# Revit family: Trim-Modern_Dots-Waterworks-Universal-Thermostatic_Valve
name_source: partatom
category: Plumbing Fixtures
revit_build: Autodesk Revit MEP 2014 (Build: 20140709_2115(x64)
units: mm (PartAtom-declared; Revit-internal decimal feet)

## types (32) — shared parameters
ADA Compliant = Yes
Assembly Code = C1030200
CW Connection = No
Default Elevation = 3' - 0"
Depth = 0' - 0 3/16"
HW Connection = No
Height = 0' - 3 3/4"
Keynote = 22 40 00
Length = 0' - 3 3/4"
Manufacturer = Waterworks
Product Documentation Link = http://assets.waterworks.com
Product Page URL = http://www.waterworks.com
URL = http://www.waterworks.com
Vent Connection = No
Version = 2014 - v1.0a
Warranty = http://www.waterworks.com
Waste Connection = No
‌Installation Requirements or Notes = Valve rough-in and finished wall must be completed prior to diverter valve trim installation.

## per-type parameters (varying)
| type | Constraint | ControlM | Description | Finish | Model | Model SKU | Product Name | Three Way Diverter | Two Way Diverter |
| Two Way Diverter Antique Brass | 1 | 1 | Universal Two Way Diverter Valve Trim for Thermostatic in Antique Brass | Metal - Waterworks - Antique Brass | UN2TM1 | 05-22928-42878 | Universal Two Way Diverter Valve Trim for Thermostatic in Antique Brass | No | Yes |
| Two Way Diverter Antique Copper | 1 | 2 | Universal Two Way Diverter Valve Trim for Thermostatic in Antique Copper | Metal - Waterworks - Antique Copper | UN2TM1 | 05-36529-58078 | Universal Two Way Diverter Valve Trim for Thermostatic in Antique Copper | No | Yes |
| Two Way Diverter Architectural Bronze | 1 | 3 | Universal Two Way Diverter Valve Trim for Thermostatic in Architectural Bronze | Metal - Waterworks - Architectural Bronze | UN2TM1 | 05-01338-41785 | Universal Two Way Diverter Valve Trim for Thermostatic in Architectural Bronze | No | Yes |
| Two Way Diverter Burnished Brass | 1 | 4 | Universal Two Way Diverter Valve Trim for Thermostatic in Burnished Brass | Metal - Waterworks - Burnished Brass | UN2TM1 | 05-19937-36672 | Universal Two Way Diverter Valve Trim for Thermostatic in Burnished Brass | No | Yes |
| Two Way Diverter Burnished Nickel | 1 | 5 | Universal Two Way Diverter Valve Trim for Thermostatic in Burnished Nickel | Metal - Waterworks - Burnished Nickel | UN2TM1 | 05-37655-42558 | Universal Two Way Diverter Valve Trim for Thermostatic in Burnished Nickel | No | Yes |
| Two Way Diverter Carbon | 1 | 6 | Universal Two Way Diverter Valve Trim for Thermostatic in Carbon | Metal - Waterworks - Carbon | UN2TM1 | 05-09789-66498 | Universal Two Way Diverter Valve Trim for Thermostatic in Carbon | No | Yes |
| Two Way Diverter Chrome | 1 | 7 | Universal Two Way Diverter Valve Trim for Thermostatic in Chrome | Metal - Waterworks - Chrome | UN2TM1 | 05-77762-57694 | Universal Two Way Diverter Valve Trim for Thermostatic in Chrome | No | Yes |
| Two Way Diverter Gold | 1 | 8 | Universal Two Way Diverter Valve Trim for Thermostatic in Gold | Metal - Waterworks - Gold | UN2TM1 | 05-06073-46610 | Universal Two Way Diverter Valve Trim for Thermostatic in Gold | No | Yes |
| Two Way Diverter Matte Gold | 1 | 9 | Universal Two Way Diverter Valve Trim for Thermostatic in Matte Gold | Metal - Waterworks - Matte Gold | UN2TM1 | 05-86456-21182 | Universal Two Way Diverter Valve Trim for Thermostatic in Matte Gold | No | Yes |
| Two Way Diverter Matte Nickel | 1 | 10 | Universal Two Way Diverter Valve Trim for Thermostatic in Matte Nickel | Metal - Waterworks - Matte Nickel | UN2TM1 | 05-69705-07265 | Universal Two Way Diverter Valve Trim for Thermostatic in Matte Nickel | No | Yes |
| Two Way Diverter Nickel | 1 | 11 | Universal Two Way Diverter Valve Trim for Thermostatic in Nickel | Metal - Waterworks - Nickel | UN2TM1 | 05-23391-97102 | Universal Two Way Diverter Valve Trim for Thermostatic in Nickel | No | Yes |
| Two Way Diverter Pewter | 1 | 12 | Universal Two Way Diverter Valve Trim for Thermostatic in Pewter | Metal - Waterworks - Pewter | UN2TM1 | 05-39654-76002 | Universal Two Way Diverter Valve Trim for Thermostatic in Pewter | No | Yes |
| Two Way Diverter Shiny Copper | 1 | 13 | Universal Two Way Diverter Valve Trim for Thermostatic in Shiny Copper | Metal - Waterworks - Shiny Copper | UN2TM1 | 05-16015-99898 | Universal Two Way Diverter Valve Trim for Thermostatic in Shiny Copper | No | Yes |
| Two Way Diverter Sovereign | 1 | 14 | Universal Two Way Diverter Valve Trim for Thermostatic in Sovereign | Metal - Waterworks - Sovereign | UN2TM1 | 05-23788-55453 | Universal Two Way Diverter Valve Trim for Thermostatic in Sovereign | No | Yes |
| Two Way Diverter Unlacquered Brass | 1 | 15 | Universal Two Way Diverter Valve Trim for Thermostatic in Unlacquered Brass | Metal - Waterworks - Unlacquered Brass | UN2TM1 | 05-95064-94585 | Universal Two Way Diverter Valve Trim for Thermostatic in Unlacquered Brass | No | Yes |
| Two Way Diverter Vintage Brass | 1 | 16 | Universal Two Way Diverter Valve Trim for Thermostatic in Vintage Brass | Metal - Waterworks - Vintage Brass | UN2TM1 | 05-02148-62719 | Universal Two Way Diverter Valve Trim for Thermostatic in Vintage Brass | No | Yes |
| Three Way Diverter Antique Brass | 2 | 1 | Universal Three Way Diverter Valve Trim for Thermostatic in Antique Brass | Metal - Waterworks - Antique Brass | UN3TM1 | 05-97624-32459 | Universal Three Way Diverter Valve Trim for Thermostatic in Antique Brass | Yes | No |
| Three Way Diverter Antique Copper | 2 | 2 | Universal Three Way Diverter Valve Trim for Thermostatic in Antique Copper | Metal - Waterworks - Antique Copper | UN3TM1 | 05-24403-44214 | Universal Three Way Diverter Valve Trim for Thermostatic in Antique Copper | Yes | No |
| Three Way Diverter Architectural Bronze | 2 | 3 | Universal Three Way Diverter Valve Trim for Thermostatic in Architectural Bronze | Metal - Waterworks - Architectural Bronze | UN3TM1 | 05-26782-24273 | Universal Three Way Diverter Valve Trim for Thermostatic in Architectural Bronze | Yes | No |
| Three Way Diverter Burnished Brass | 2 | 4 | Universal Three Way Diverter Valve Trim for Thermostatic in Burnished Brass | Metal - Waterworks - Burnished Brass | UN3TM1 | 05-42249-10130 | Universal Three Way Diverter Valve Trim for Thermostatic in Burnished Brass | Yes | No |
| Three Way Diverter Burnished Nickel | 2 | 5 | Universal Three Way Diverter Valve Trim for Thermostatic in Burnished Nickel | Metal - Waterworks - Burnished Nickel | UN3TM1 | 05-16267-54630 | Universal Three Way Diverter Valve Trim for Thermostatic in Burnished Nickel | Yes | No |
| Three Way Diverter Carbon | 2 | 6 | Universal Three Way Diverter Valve Trim for Thermostatic in Carbon | Metal - Waterworks - Carbon | UN3TM1 | 05-61901-60749 | Universal Three Way Diverter Valve Trim for Thermostatic in Carbon | Yes | No |
| Three Way Diverter Chrome | 2 | 7 | Universal Three Way Diverter Valve Trim for Thermostatic in Chrome | Metal - Waterworks - Chrome | UN3TM1 | 05-28288-44779 | Universal Three Way Diverter Valve Trim for Thermostatic in Chrome | Yes | No |
| Three Way Diverter Gold | 2 | 8 | Universal Three Way Diverter Valve Trim for Thermostatic in Gold | Metal - Waterworks - Gold | UN3TM1 | 05-28626-16723 | Universal Three Way Diverter Valve Trim for Thermostatic in Gold | Yes | No |
| Three Way Diverter Matte Gold | 2 | 9 | Universal Three Way Diverter Valve Trim for Thermostatic in Matte Gold | Metal - Waterworks - Matte Gold | UN3TM1 | 05-66451-82811 | Universal Three Way Diverter Valve Trim for Thermostatic in Matte Gold | Yes | No |
| Three Way Diverter Matte Nickel | 2 | 10 | Universal Three Way Diverter Valve Trim for Thermostatic in Matte Nickel | Metal - Waterworks - Matte Nickel | UN3TM1 | 05-37432-92778 | Universal Three Way Diverter Valve Trim for Thermostatic in Matte Nickel | Yes | No |
| Three Way Diverter Nickel | 2 | 11 | Universal Three Way Diverter Valve Trim for Thermostatic in Nickel | Metal - Waterworks - Nickel | UN3TM1 | 05-60743-83830 | Universal Three Way Diverter Valve Trim for Thermostatic in Nickel | Yes | No |
| Three Way Diverter Pewter | 2 | 12 | Universal Three Way Diverter Valve Trim for Thermostatic in Pewter | Metal - Waterworks - Pewter | UN3TM1 | 05-32332-66926 | Universal Three Way Diverter Valve Trim for Thermostatic in Pewter | Yes | No |
| Three Way Diverter Shiny Copper | 2 | 13 | Universal Three Way Diverter Valve Trim for Thermostatic in Shiny Copper | Metal - Waterworks - Shiny Copper | UN3TM1 | 05-24296-38095 | Universal Three Way Diverter Valve Trim for Thermostatic in Shiny Copper | Yes | No |
| Three Way Diverter Sovereign | 2 | 14 | Universal Three Way Diverter Valve Trim for Thermostatic in Sovereign | Metal - Waterworks - Sovereign | UN3TM1 | 05-04033-72635 | Universal Three Way Diverter Valve Trim for Thermostatic in Sovereign | Yes | No |
| Three Way Diverter Unlacquered Brass | 2 | 15 | Universal Three Way Diverter Valve Trim for Thermostatic in Unlacquered Brass | Metal - Waterworks - Unlacquered Brass | UN3TM1 | 05-59559-48970 | Universal Three Way Diverter Valve Trim for Thermostatic in Unlacquered Brass | Yes | No |
| Three Way Diverter Vintage Brass | 2 | 16 | Universal Three Way Diverter Valve Trim for Thermostatic in Vintage Brass | Metal - Waterworks - Vintage Brass | UN3TM1 | 05-36514-94431 | Universal Three Way Diverter Valve Trim for Thermostatic in Vintage Brass | Yes | No |

## geometry (parser evidence)
native form markers: Sweep x6
no freeform markers — native parametric forms only
